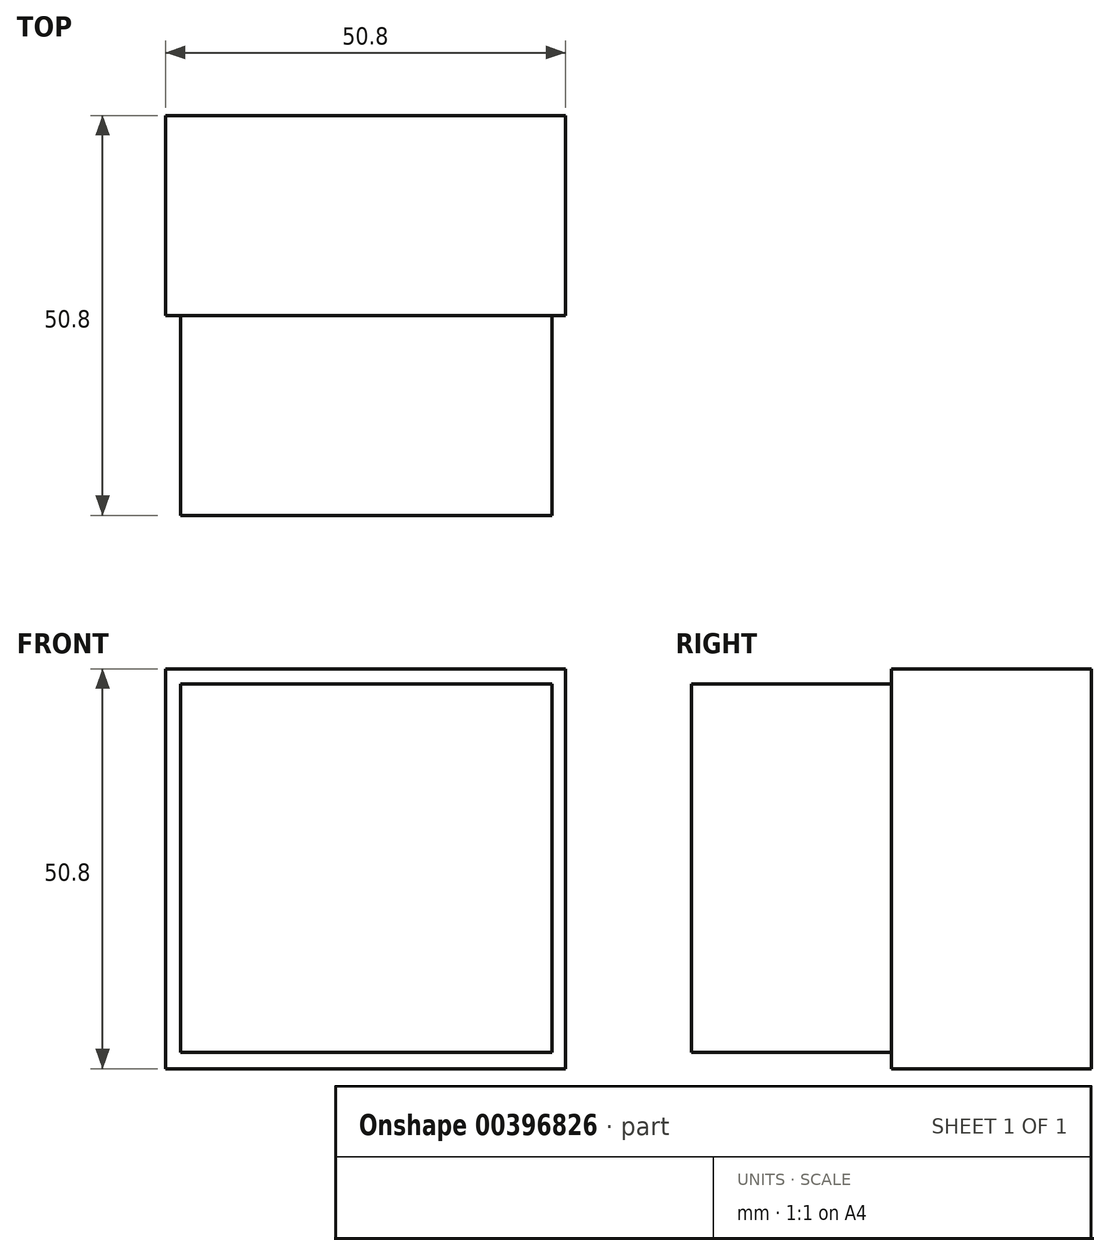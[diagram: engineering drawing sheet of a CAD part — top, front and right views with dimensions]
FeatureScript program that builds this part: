
annotation { "Feature Type Name" : "Feature", "Feature Type Description" : "" }
export const myFeature = defineFeature(function(context is Context, id is Id, definition is map)
    precondition{}
    {
        {
            var Q0;
            Q0=qCreatedBy(makeId("Front.planeOp"),FACE);
            var sketch = newSketch(context, id + "F0", { "sketchPlane" : qUnion([Q0])});
            skLineSegment(sketch, "E0.bottom", {"start": v(6.88, 4.4) * mm, "end": v(-43.92, 4.4) * mm});
            skLineSegment(sketch, "E0.top", {"start": v(6.88, 55.2) * mm, "end": v(-43.92, 55.2) * mm});
            skLineSegment(sketch, "E0.left", {"start": v(6.88, 4.4) * mm, "end": v(6.88, 55.2) * mm});
            skLineSegment(sketch, "E0.right", {"start": v(-43.92, 4.4) * mm, "end": v(-43.92, 55.2) * mm});
            skSolve(sketch);
        }
        {
            var Q0;
            Q0 = qSketchRegion(id + "F0", true);
            extrude(context, id + "F1", {"entities" : qUnion([Q0]), "depth" : 25.4 * mm});
        }
        {
            var Q0;
            Q0=makeQuery(id+"F1.opExtrude","CAP_FACE",FACE,{"disambiguationData":[OSD([sQuery(id+"F0.wireOp",EDGE,"E0.bottom"),sQuery(id+"F0.wireOp",EDGE,"E0.top"),sQuery(id+"F0.wireOp",EDGE,"E0.left"),sQuery(id+"F0.wireOp",EDGE,"E0.right")])],"isStart":false});
            var sketch = newSketch(context, id + "F2", { "sketchPlane" : qUnion([Q0])});
            skLineSegment(sketch, "E1.bottom", {"start": v(-42.01, 53.28) * mm, "end": v(5.16, 53.28) * mm});
            skLineSegment(sketch, "E1.top", {"start": v(-42.01, 6.5) * mm, "end": v(5.16, 6.5) * mm});
            skLineSegment(sketch, "E1.left", {"start": v(-42.01, 53.28) * mm, "end": v(-42.01, 6.5) * mm});
            skLineSegment(sketch, "E1.right", {"start": v(5.16, 53.28) * mm, "end": v(5.16, 6.5) * mm});
            skLineSegment(sketch, "E2.bottom", {"start": v(81.7, 40.34) * mm, "end": v(81.48, 40.34) * mm});
            skLineSegment(sketch, "E2.top", {"start": v(81.7, 34.55) * mm, "end": v(81.48, 34.55) * mm});
            skLineSegment(sketch, "E2.left", {"start": v(81.7, 40.34) * mm, "end": v(81.7, 34.55) * mm});
            skLineSegment(sketch, "E2.right", {"start": v(81.48, 40.34) * mm, "end": v(81.48, 34.55) * mm});
            skSolve(sketch);
        }
        {
            var Q0;
            Q0=makeQuery(id+"F2.imprint","IMPRINT",FACE,{"disambiguationData":[TD([[makeQuery(id+"F2.imprint","IMPRINT",EDGE,{"derivedFrom":sQuery(id+"F2.wireOp",EDGE,"E1.bottom")}),-1.0]])]});
            extrude(context, id + "F3", {"entities" : qUnion([Q0]), "operationType" : NewBodyOperationType.ADD, "depth" : 25.4 * mm});
        }
    });
